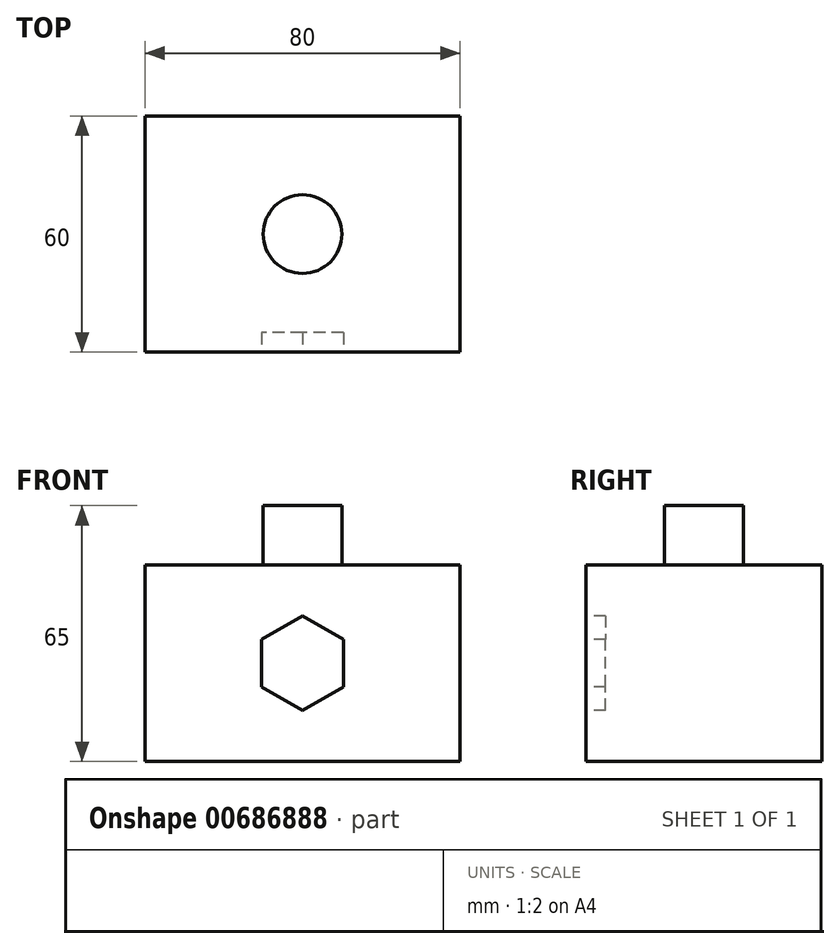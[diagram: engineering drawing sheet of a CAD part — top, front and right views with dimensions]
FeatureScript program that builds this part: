
annotation { "Feature Type Name" : "Feature", "Feature Type Description" : "" }
export const myFeature = defineFeature(function(context is Context, id is Id, definition is map)
    precondition{}
    {
        {
            var Q0;
            Q0=qCreatedBy(makeId("Top.planeOp"),FACE);
            var sketch = newSketch(context, id + "F0", { "sketchPlane" : qUnion([Q0])});
            skLineSegment(sketch, "E0.bottom", {"start": v(-40, 30) * mm, "end": v(40, 30) * mm});
            skLineSegment(sketch, "E0.top", {"start": v(-40, -30) * mm, "end": v(40, -30) * mm});
            skLineSegment(sketch, "E0.left", {"start": v(-40, 30) * mm, "end": v(-40, -30) * mm});
            skLineSegment(sketch, "E0.right", {"start": v(40, 30) * mm, "end": v(40, -30) * mm});
            skPoint(sketch, "E0.middle", {"position": v(0, 0) * mm});
            skSolve(sketch);
        }
        {
            var Q0;
            Q0 = qSketchRegion(id + "F0", true);
            extrude(context, id + "F1", {"entities" : qUnion([Q0]), "depth" : 50 * mm, "offsetDistance" : 25 * mm});
        }
        {
            var Q0;
            Q0=makeQuery(id+"F1.opExtrude","CAP_FACE",FACE,{"disambiguationData":[OSD([sQuery(id+"F0.wireOp",EDGE,"E0.bottom"),sQuery(id+"F0.wireOp",EDGE,"E0.top"),sQuery(id+"F0.wireOp",EDGE,"E0.left"),sQuery(id+"F0.wireOp",EDGE,"E0.right")])],"isStart":false});
            var sketch = newSketch(context, id + "F2", { "sketchPlane" : qUnion([Q0])});
            skCircle(sketch, "E1", {"center": v(0, 0) * mm, "radius": 10 * mm});
            skSolve(sketch);
        }
        {
            var Q0;
            Q0=makeQuery(id+"F2.imprint","IMPRINT",FACE,{"disambiguationData":[TD([[makeQuery(id+"F2.imprint","IMPRINT",EDGE,{"derivedFrom":sQuery(id+"F2.wireOp",EDGE,"E1")}),1.0]])]});
            extrude(context, id + "F3", {"entities" : qUnion([Q0]), "operationType" : NewBodyOperationType.ADD, "depth" : 15 * mm, "offsetDistance" : 25 * mm});
        }
        {
            var Q0;
            Q0=makeQuery(id+"F1.opExtrude","SWEPT_FACE",FACE,{"disambiguationData":[OSD([sQuery(id+"F0.wireOp",EDGE,"E0.top")])]});
            var sketch = newSketch(context, id + "F4", { "sketchPlane" : qUnion([Q0])});
            skCircle(sketch, "E2.cCircle", {"center": v(0, 25) * mm, "radius": 10.4 * mm, "construction": true});
            skLineSegment(sketch, "E2.0", {"start": v(-10.4, 19) * mm, "end": v(-10.4, 31) * mm});
            skLineSegment(sketch, "E2.1", {"start": v(-10.4, 31) * mm, "end": v(0, 37) * mm});
            skLineSegment(sketch, "E2.2", {"start": v(0, 37) * mm, "end": v(10.4, 31) * mm});
            skLineSegment(sketch, "E2.3", {"start": v(10.4, 31) * mm, "end": v(10.4, 19) * mm});
            skLineSegment(sketch, "E2.4", {"start": v(10.4, 19) * mm, "end": v(0, 13) * mm});
            skLineSegment(sketch, "E2.5", {"start": v(0, 13) * mm, "end": v(-10.4, 19) * mm});
            skPoint(sketch, "E2.0.midPoint", {"position": v(-10.4, 25) * mm});
            skSolve(sketch);
        }
        {
            var Q0;
            Q0=makeQuery(id+"F4.imprint","IMPRINT",FACE,{"disambiguationData":[TD([[makeQuery(id+"F4.imprint","IMPRINT",EDGE,{"derivedFrom":sQuery(id+"F4.wireOp",EDGE,"E2.0")}),-1.0]])]});
            extrude(context, id + "F5", {"entities" : qUnion([Q0]), "operationType" : NewBodyOperationType.REMOVE, "oppositeDirection" : true, "depth" : 5 * mm, "offsetDistance" : 25 * mm});
        }
    });
